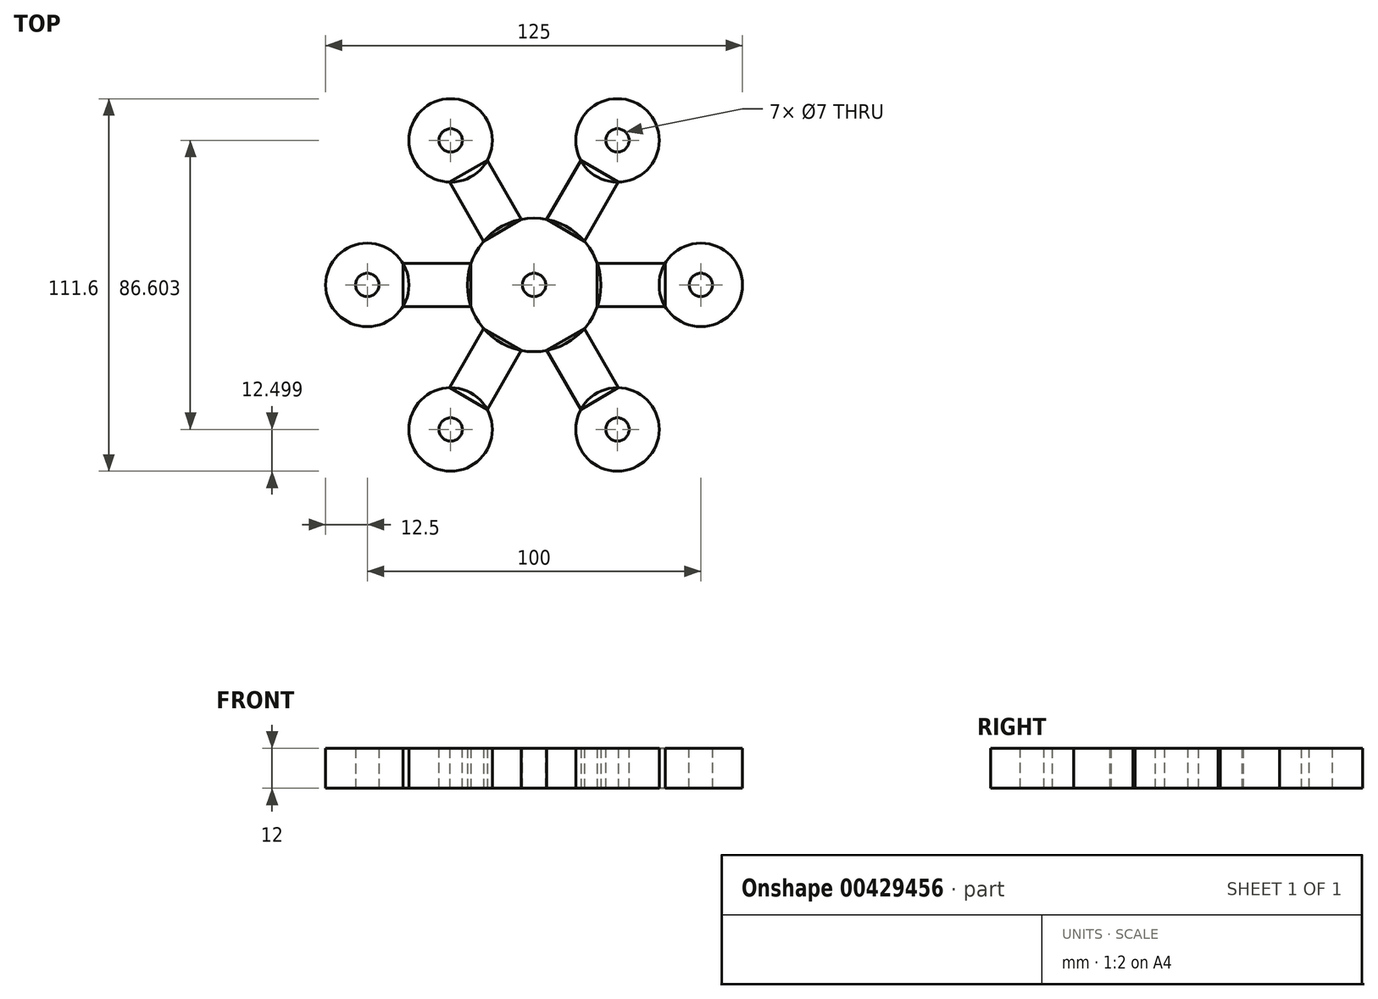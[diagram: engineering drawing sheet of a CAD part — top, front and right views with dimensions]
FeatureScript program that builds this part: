
annotation { "Feature Type Name" : "Feature", "Feature Type Description" : "" }
export const myFeature = defineFeature(function(context is Context, id is Id, definition is map)
    precondition{}
    {
        {
            var Q0;
            Q0=qCreatedBy(makeId("Top.planeOp"),FACE);
            var sketch = newSketch(context, id + "F0", { "sketchPlane" : qUnion([Q0])});
            skLineSegment(sketch, "E0", {"start": v(0, 0) * mm, "end": v(50, 0) * mm});
            skLineSegment(sketch, "E1", {"start": v(0, 0) * mm, "end": v(25, 43.3) * mm});
            skLineSegment(sketch, "E2", {"start": v(0, 0) * mm, "end": v(-25, 43.3) * mm});
            skLineSegment(sketch, "E3", {"start": v(0, 0) * mm, "end": v(-50, 0) * mm});
            skLineSegment(sketch, "E4", {"start": v(0, 0) * mm, "end": v(-25, -43.3) * mm});
            skLineSegment(sketch, "E5", {"start": v(0, 0) * mm, "end": v(25, -43.3) * mm});
            skSolve(sketch);
        }
        {
            var Q0;
            Q0=qCreatedBy(makeId("Top.planeOp"),FACE);
            var sketch = newSketch(context, id + "F1", { "sketchPlane" : qUnion([Q0])});
            skCircle(sketch, "E6", {"center": v(-25, 43.3) * mm, "radius": 12.5 * mm});
            skSolve(sketch);
        }
        {
            var Q0;
            Q0=qCreatedBy(makeId("Top.planeOp"),FACE);
            var sketch = newSketch(context, id + "F2", { "sketchPlane" : qUnion([Q0])});
            skCircle(sketch, "E7", {"center": v(25, 43.3) * mm, "radius": 12.5 * mm});
            skSolve(sketch);
        }
        {
            var Q0;
            Q0=qCreatedBy(makeId("Top.planeOp"),FACE);
            var sketch = newSketch(context, id + "F3", { "sketchPlane" : qUnion([Q0])});
            skCircle(sketch, "E8", {"center": v(50, 0) * mm, "radius": 12.5 * mm});
            skSolve(sketch);
        }
        {
            var Q0;
            Q0=qCreatedBy(makeId("Top.planeOp"),FACE);
            var sketch = newSketch(context, id + "F4", { "sketchPlane" : qUnion([Q0])});
            skCircle(sketch, "E9", {"center": v(25, -43.3) * mm, "radius": 12.5 * mm});
            skSolve(sketch);
        }
        {
            var Q0;
            Q0=qCreatedBy(makeId("Top.planeOp"),FACE);
            var sketch = newSketch(context, id + "F5", { "sketchPlane" : qUnion([Q0])});
            skCircle(sketch, "E10", {"center": v(-25, -43.3) * mm, "radius": 12.5 * mm});
            skSolve(sketch);
        }
        {
            var Q0;
            Q0=qCreatedBy(makeId("Top.planeOp"),FACE);
            var sketch = newSketch(context, id + "F6", { "sketchPlane" : qUnion([Q0])});
            skCircle(sketch, "E11", {"center": v(-50, 0) * mm, "radius": 12.5 * mm});
            skSolve(sketch);
        }
        {
            var Q0;
            Q0=qCreatedBy(makeId("Top.planeOp"),FACE);
            var sketch = newSketch(context, id + "F7", { "sketchPlane" : qUnion([Q0])});
            skCircle(sketch, "E12", {"center": v(0, 0) * mm, "radius": 20 * mm});
            skSolve(sketch);
        }
        {
            var Q0;
            Q0=qCreatedBy(makeId("Top.planeOp"),FACE);
            var sketch = newSketch(context, id + "F8", { "sketchPlane" : qUnion([Q0])});
            skLineSegment(sketch, "E13.bottom", {"start": v(-14.03, -37.3) * mm, "end": v(-3.83, -19.63) * mm});
            skLineSegment(sketch, "E13.top", {"start": v(-25.3, -30.8) * mm, "end": v(-15.09, -13.13) * mm});
            skLineSegment(sketch, "E13.left", {"start": v(-25.3, -30.8) * mm, "end": v(-14.03, -37.3) * mm});
            skLineSegment(sketch, "E13.right", {"start": v(-15.09, -13.13) * mm, "end": v(-3.83, -19.63) * mm});
            skSolve(sketch);
        }
        {
            var Q0;
            Q0=qCreatedBy(makeId("Top.planeOp"),FACE);
            var sketch = newSketch(context, id + "F9", { "sketchPlane" : qUnion([Q0])});
            skLineSegment(sketch, "E14", {"start": v(14.03, -37.3) * mm, "end": v(25.3, -30.8) * mm});
            skLineSegment(sketch, "E15", {"start": v(25.3, -30.8) * mm, "end": v(15.09, -13.13) * mm});
            skLineSegment(sketch, "E16", {"start": v(15.09, -13.13) * mm, "end": v(3.83, -19.63) * mm});
            skLineSegment(sketch, "E17", {"start": v(3.83, -19.63) * mm, "end": v(14.03, -37.3) * mm});
            skSolve(sketch);
        }
        {
            var Q0;
            Q0=qCreatedBy(makeId("Top.planeOp"),FACE);
            var sketch = newSketch(context, id + "F10", { "sketchPlane" : qUnion([Q0])});
            skLineSegment(sketch, "E18", {"start": v(-25.3, 30.8) * mm, "end": v(-15.09, 13.13) * mm});
            skLineSegment(sketch, "E19", {"start": v(-15.09, 13.13) * mm, "end": v(-3.83, 19.63) * mm});
            skLineSegment(sketch, "E20", {"start": v(-3.83, 19.63) * mm, "end": v(-14.03, 37.3) * mm});
            skLineSegment(sketch, "E21", {"start": v(-14.03, 37.3) * mm, "end": v(-25.3, 30.8) * mm});
            skSolve(sketch);
        }
        {
            var Q0;
            Q0=qCreatedBy(makeId("Top.planeOp"),FACE);
            var sketch = newSketch(context, id + "F11", { "sketchPlane" : qUnion([Q0])});
            skLineSegment(sketch, "E22", {"start": v(14.03, 37.3) * mm, "end": v(3.83, 19.63) * mm});
            skLineSegment(sketch, "E23", {"start": v(3.83, 19.63) * mm, "end": v(15.09, 13.13) * mm});
            skLineSegment(sketch, "E24", {"start": v(15.09, 13.13) * mm, "end": v(25.3, 30.8) * mm});
            skLineSegment(sketch, "E25", {"start": v(25.3, 30.8) * mm, "end": v(14.03, 37.3) * mm});
            skSolve(sketch);
        }
        {
            var Q0;
            Q0=qCreatedBy(makeId("Top.planeOp"),FACE);
            var sketch = newSketch(context, id + "F12", { "sketchPlane" : qUnion([Q0])});
            skLineSegment(sketch, "E26", {"start": v(-39.32, 6.5) * mm, "end": v(-18.91, 6.5) * mm});
            skLineSegment(sketch, "E27", {"start": v(-18.91, 6.5) * mm, "end": v(-18.91, -6.5) * mm});
            skLineSegment(sketch, "E28", {"start": v(-18.91, -6.5) * mm, "end": v(-39.32, -6.5) * mm});
            skLineSegment(sketch, "E29", {"start": v(-39.32, -6.5) * mm, "end": v(-39.32, 6.5) * mm});
            skSolve(sketch);
        }
        {
            var Q0;
            Q0=qCreatedBy(makeId("Top.planeOp"),FACE);
            var sketch = newSketch(context, id + "F13", { "sketchPlane" : qUnion([Q0])});
            skLineSegment(sketch, "E30", {"start": v(18.91, 6.5) * mm, "end": v(39.32, 6.5) * mm});
            skLineSegment(sketch, "E31", {"start": v(39.32, 6.5) * mm, "end": v(39.32, -6.5) * mm});
            skLineSegment(sketch, "E32", {"start": v(39.32, -6.5) * mm, "end": v(18.91, -6.5) * mm});
            skLineSegment(sketch, "E33", {"start": v(18.91, -6.5) * mm, "end": v(18.91, 6.5) * mm});
            skSolve(sketch);
        }
        {
            var Q0;
            Q0=makeQuery(id+"F1.imprint","IMPRINT",FACE,{"disambiguationData":[TD([[makeQuery(id+"F1.imprint","IMPRINT",EDGE,{"derivedFrom":sQuery(id+"F1.wireOp",EDGE,"E6")}),1.0]])]});
            var Q1;
            Q1=makeQuery(id+"F10.imprint","IMPRINT",FACE,{"disambiguationData":[TD([[makeQuery(id+"F10.imprint","IMPRINT",EDGE,{"derivedFrom":sQuery(id+"F10.wireOp",EDGE,"E18")}),1.0]])]});
            var Q2;
            Q2=makeQuery(id+"F2.imprint","IMPRINT",FACE,{"disambiguationData":[TD([[makeQuery(id+"F2.imprint","IMPRINT",EDGE,{"derivedFrom":sQuery(id+"F2.wireOp",EDGE,"E7")}),1.0]])]});
            var Q3;
            Q3=makeQuery(id+"F11.imprint","IMPRINT",FACE,{"disambiguationData":[TD([[makeQuery(id+"F11.imprint","IMPRINT",EDGE,{"derivedFrom":sQuery(id+"F11.wireOp",EDGE,"E22")}),1.0]])]});
            var Q4;
            Q4=makeQuery(id+"F7.imprint","IMPRINT",FACE,{"disambiguationData":[TD([[makeQuery(id+"F7.imprint","IMPRINT",EDGE,{"derivedFrom":sQuery(id+"F7.wireOp",EDGE,"E12")}),1.0]])]});
            var Q5;
            Q5=makeQuery(id+"F13.imprint","IMPRINT",FACE,{"disambiguationData":[TD([[makeQuery(id+"F13.imprint","IMPRINT",EDGE,{"derivedFrom":sQuery(id+"F13.wireOp",EDGE,"E30")}),-1.0]])]});
            var Q6;
            Q6=makeQuery(id+"F3.imprint","IMPRINT",FACE,{"disambiguationData":[TD([[makeQuery(id+"F3.imprint","IMPRINT",EDGE,{"derivedFrom":sQuery(id+"F3.wireOp",EDGE,"E8")}),1.0]])]});
            var Q7;
            Q7=makeQuery(id+"F4.imprint","IMPRINT",FACE,{"disambiguationData":[TD([[makeQuery(id+"F4.imprint","IMPRINT",EDGE,{"derivedFrom":sQuery(id+"F4.wireOp",EDGE,"E9")}),1.0]])]});
            var Q8;
            Q8=makeQuery(id+"F9.imprint","IMPRINT",FACE,{"disambiguationData":[TD([[makeQuery(id+"F9.imprint","IMPRINT",EDGE,{"derivedFrom":sQuery(id+"F9.wireOp",EDGE,"E14")}),1.0]])]});
            var Q9;
            Q9=makeQuery(id+"F5.imprint","IMPRINT",FACE,{"disambiguationData":[TD([[makeQuery(id+"F5.imprint","IMPRINT",EDGE,{"derivedFrom":sQuery(id+"F5.wireOp",EDGE,"E10")}),1.0]])]});
            var Q10;
            Q10=makeQuery(id+"F8.imprint","IMPRINT",FACE,{"disambiguationData":[TD([[makeQuery(id+"F8.imprint","IMPRINT",EDGE,{"derivedFrom":sQuery(id+"F8.wireOp",EDGE,"E13.bottom")}),1.0]])]});
            var Q11;
            Q11=makeQuery(id+"F12.imprint","IMPRINT",FACE,{"disambiguationData":[TD([[makeQuery(id+"F12.imprint","IMPRINT",EDGE,{"derivedFrom":sQuery(id+"F12.wireOp",EDGE,"E26")}),-1.0]])]});
            var Q12;
            Q12=makeQuery(id+"F6.imprint","IMPRINT",FACE,{"disambiguationData":[TD([[makeQuery(id+"F6.imprint","IMPRINT",EDGE,{"derivedFrom":sQuery(id+"F6.wireOp",EDGE,"E11")}),1.0]])]});
            extrude(context, id + "F14", {"entities" : qUnion([Q0, Q1, Q2, Q3, Q4, Q5, Q6, Q7, Q8, Q9, Q10, Q11, Q12]), "depth" : 12 * mm});
        }
        {
            var Q0;
            Q0=qCreatedBy(makeId("Top.planeOp"),FACE);
            var sketch = newSketch(context, id + "F15", { "sketchPlane" : qUnion([Q0])});
            skPoint(sketch, "E34", {"position": v(-50, 0) * mm});
            skCircle(sketch, "E35", {"center": v(-50, 0) * mm, "radius": 3.5 * mm});
            skSolve(sketch);
        }
        {
            var Q0;
            Q0 = qSketchRegion(id + "F15", true);
            extrude(context, id + "F16", {"entities" : qUnion([Q0]), "operationType" : NewBodyOperationType.REMOVE, "depth" : 18.8 * mm, "hasSecondDirection" : true, "secondDirectionOppositeDirection" : true, "secondDirectionDepth" : 25 * mm});
        }
        {
            var Q0;
            Q0=qCreatedBy(makeId("Top.planeOp"),FACE);
            var sketch = newSketch(context, id + "F17", { "sketchPlane" : qUnion([Q0])});
            skPoint(sketch, "E36", {"position": v(-25, 43.3) * mm});
            skCircle(sketch, "E37", {"center": v(-25, 43.3) * mm, "radius": 3.5 * mm});
            skSolve(sketch);
        }
        {
            var Q0;
            Q0=makeQuery(id+"F17.imprint","IMPRINT",FACE,{"disambiguationData":[TD([[makeQuery(id+"F17.imprint","IMPRINT",EDGE,{"derivedFrom":sQuery(id+"F17.wireOp",EDGE,"E37")}),1.0]])]});
            var Q1;
            Q1=sQuery(id+"F17.wireOp",EDGE,"E37");
            extrude(context, id + "F18", {"entities" : qUnion([Q0]), "operationType" : NewBodyOperationType.REMOVE, "surfaceEntities" : qUnion([Q1]), "oppositeDirection" : true, "depth" : 25 * mm, "hasSecondDirection" : true, "secondDirectionOppositeDirection" : false, "secondDirectionDepth" : 25 * mm});
        }
        {
            var Q0;
            Q0=qCreatedBy(makeId("Top.planeOp"),FACE);
            var sketch = newSketch(context, id + "F19", { "sketchPlane" : qUnion([Q0])});
            skPoint(sketch, "E38", {"position": v(25, 43.3) * mm});
            skCircle(sketch, "E39", {"center": v(25, 43.3) * mm, "radius": 3.5 * mm});
            skSolve(sketch);
        }
        {
            var Q0;
            Q0 = qSketchRegion(id + "F19", true);
            extrude(context, id + "F20", {"entities" : qUnion([Q0]), "operationType" : NewBodyOperationType.REMOVE, "oppositeDirection" : true, "depth" : 25 * mm, "hasSecondDirection" : true, "secondDirectionOppositeDirection" : false, "secondDirectionDepth" : 25 * mm});
        }
        {
            var Q0;
            Q0=qCreatedBy(makeId("Top.planeOp"),FACE);
            var sketch = newSketch(context, id + "F21", { "sketchPlane" : qUnion([Q0])});
            skPoint(sketch, "E40", {"position": v(50, 0) * mm});
            skCircle(sketch, "E41", {"center": v(50, 0) * mm, "radius": 3.5 * mm});
            skSolve(sketch);
        }
        {
            var Q0;
            Q0 = qSketchRegion(id + "F21", true);
            extrude(context, id + "F22", {"entities" : qUnion([Q0]), "operationType" : NewBodyOperationType.REMOVE, "oppositeDirection" : true, "depth" : 25 * mm, "hasSecondDirection" : true, "secondDirectionOppositeDirection" : false, "secondDirectionDepth" : 25 * mm});
        }
        {
            var Q0;
            Q0=qCreatedBy(makeId("Top.planeOp"),FACE);
            var sketch = newSketch(context, id + "F23", { "sketchPlane" : qUnion([Q0])});
            skPoint(sketch, "E42", {"position": v(25, -43.3) * mm});
            skCircle(sketch, "E43", {"center": v(25, -43.3) * mm, "radius": 3.5 * mm});
            skSolve(sketch);
        }
        {
            var Q0;
            Q0 = qSketchRegion(id + "F23", true);
            extrude(context, id + "F24", {"entities" : qUnion([Q0]), "operationType" : NewBodyOperationType.REMOVE, "oppositeDirection" : true, "depth" : 25 * mm, "hasSecondDirection" : true, "secondDirectionOppositeDirection" : false, "secondDirectionDepth" : 25 * mm});
        }
        {
            var Q0;
            Q0=qCreatedBy(makeId("Top.planeOp"),FACE);
            var sketch = newSketch(context, id + "F25", { "sketchPlane" : qUnion([Q0])});
            skPoint(sketch, "E44", {"position": v(-25, -43.3) * mm});
            skCircle(sketch, "E45", {"center": v(-25, -43.3) * mm, "radius": 3.5 * mm});
            skSolve(sketch);
        }
        {
            var Q0;
            Q0 = qSketchRegion(id + "F25", true);
            extrude(context, id + "F26", {"entities" : qUnion([Q0]), "operationType" : NewBodyOperationType.REMOVE, "oppositeDirection" : true, "depth" : 25 * mm, "hasSecondDirection" : true, "secondDirectionOppositeDirection" : false, "secondDirectionDepth" : 25 * mm});
        }
        {
            var Q0;
            Q0=makeQuery(id+"F14.opExtrude","CAP_FACE",FACE,{"disambiguationData":[OSD([sQuery(id+"F5.wireOp",EDGE,"E10")])],"isStart":false});
            var sketch = newSketch(context, id + "F27", { "sketchPlane" : qUnion([Q0])});
            skCircle(sketch, "E46", {"center": v(0, 0) * mm, "radius": 3.5 * mm});
            skSolve(sketch);
        }
        {
            var Q0;
            Q0 = qSketchRegion(id + "F27", true);
            extrude(context, id + "F28", {"entities" : qUnion([Q0]), "operationType" : NewBodyOperationType.REMOVE, "oppositeDirection" : true, "depth" : 25 * mm, "hasSecondDirection" : true, "secondDirectionOppositeDirection" : false, "secondDirectionDepth" : 25 * mm});
        }
    });
